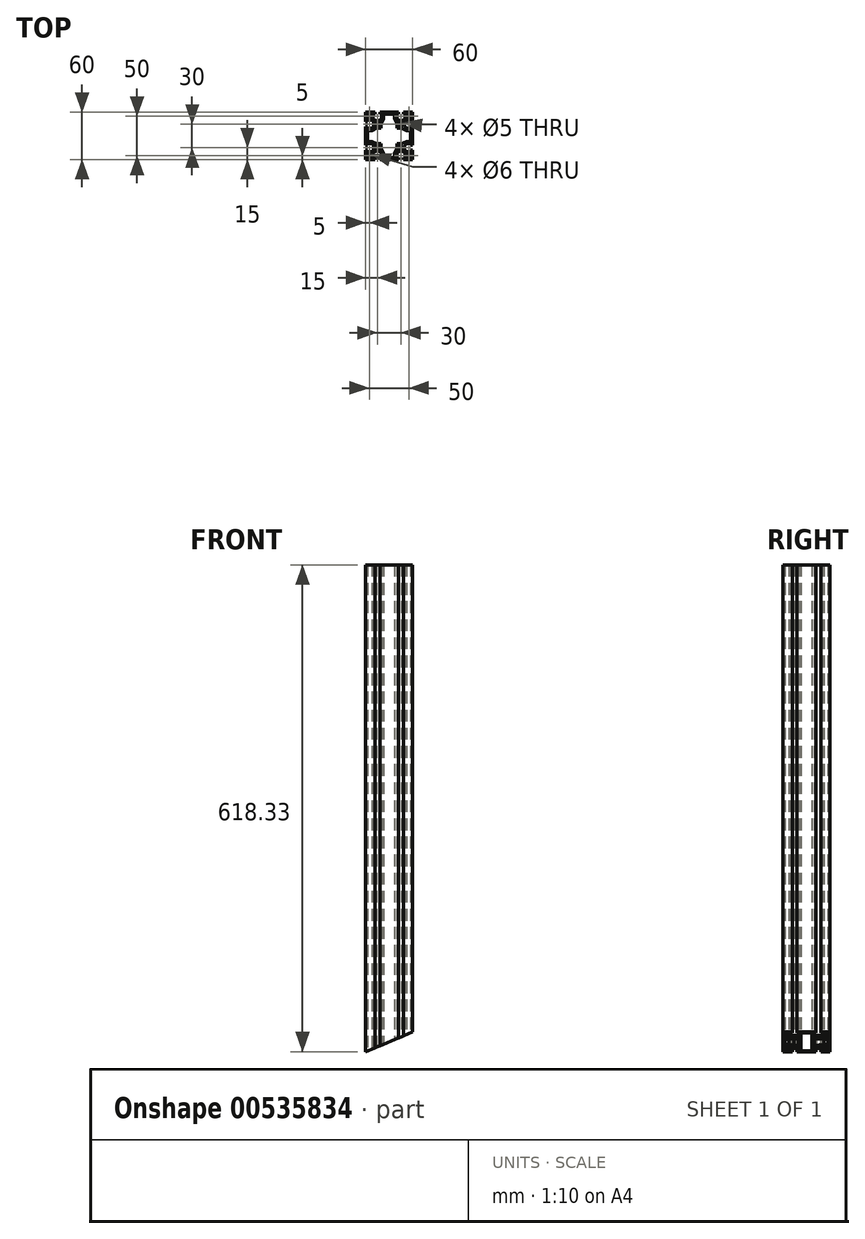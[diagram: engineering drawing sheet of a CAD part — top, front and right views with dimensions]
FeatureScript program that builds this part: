
annotation { "Feature Type Name" : "Feature", "Feature Type Description" : "" }
export const myFeature = defineFeature(function(context is Context, id is Id, definition is map)
    precondition{}
    {
        {
            var Q0;
            Q0=qCreatedBy(makeId("Top.planeOp"),FACE);
            var sketch = newSketch(context, id + "F0", { "sketchPlane" : qUnion([Q0])});
            skLineSegment(sketch, "E0.bottom", {"start": v(30, -30) * mm, "end": v(-30, -30) * mm});
            skLineSegment(sketch, "E0.top", {"start": v(30, 30) * mm, "end": v(-30, 30) * mm});
            skLineSegment(sketch, "E0.left", {"start": v(30, -30) * mm, "end": v(30, 30) * mm});
            skLineSegment(sketch, "E0.right", {"start": v(-30, -30) * mm, "end": v(-30, 30) * mm});
            skPoint(sketch, "E0.middle", {"position": v(0, 0) * mm});
            skLineSegment(sketch, "E1.top", {"start": v(-11.85, 30) * mm, "end": v(-18.15, 30) * mm});
            skLineSegment(sketch, "E1.left", {"start": v(-11.85, 27.5) * mm, "end": v(-11.85, 30) * mm});
            skLineSegment(sketch, "E1.right", {"start": v(-18.15, 27.5) * mm, "end": v(-18.15, 30) * mm});
            skPoint(sketch, "E1.middle", {"position": v(-15, 28.75) * mm});
            skLineSegment(sketch, "E2.bottom", {"start": v(-9.85, 27.5) * mm, "end": v(-11.85, 27.5) * mm});
            skLineSegment(sketch, "E2.left", {"start": v(-9.85, 27.5) * mm, "end": v(-9.85, 21.55) * mm});
            skLineSegment(sketch, "E2.right", {"start": v(-20.15, 27.5) * mm, "end": v(-20.15, 21.55) * mm});
            skPoint(sketch, "E2.middle", {"position": v(-15, 24.52) * mm});
            skArc(sketch, "E3", {"start": v(-20.15, 21.55) * mm, "mid": v(-15, 19.5) * mm, "end": v(-9.85, 21.55) * mm});
            skPoint(sketch, "E4.MirrorP", {"position": v(15, 24.52) * mm});
            skPoint(sketch, "E5.MirrorP", {"position": v(15, 28.75) * mm});
            skLineSegment(sketch, "E6.MirrorCS", {"start": v(11.85, 27.5) * mm, "end": v(11.85, 30) * mm});
            skLineSegment(sketch, "E7.MirrorCS", {"start": v(18.15, 27.5) * mm, "end": v(18.15, 30) * mm});
            skLineSegment(sketch, "E8.MirrorCS", {"start": v(9.85, 27.5) * mm, "end": v(11.85, 27.5) * mm});
            skLineSegment(sketch, "E9.MirrorCS", {"start": v(9.85, 27.5) * mm, "end": v(9.85, 21.55) * mm});
            skArc(sketch, "E10.MirrorCS", {"start": v(20.15, 21.55) * mm, "mid": v(15, 19.5) * mm, "end": v(9.85, 21.55) * mm});
            skLineSegment(sketch, "E11.MirrorCS", {"start": v(20.15, 27.5) * mm, "end": v(20.15, 21.55) * mm});
            skLineSegment(sketch, "E12.MirrorCS", {"start": v(11.85, 30) * mm, "end": v(18.15, 30) * mm});
            skLineSegment(sketch, "E13.1.0", {"start": v(27.5, 20.15) * mm, "end": v(21.55, 20.15) * mm});
            skLineSegment(sketch, "E13.1.1", {"start": v(27.5, 9.85) * mm, "end": v(21.55, 9.85) * mm});
            skArc(sketch, "E13.1.2", {"start": v(21.55, 20.15) * mm, "mid": v(19.5, 15) * mm, "end": v(21.55, 9.85) * mm});
            skLineSegment(sketch, "E13.1.3", {"start": v(27.5, -9.85) * mm, "end": v(21.55, -9.85) * mm});
            skLineSegment(sketch, "E13.1.4", {"start": v(27.5, -20.15) * mm, "end": v(21.55, -20.15) * mm});
            skPoint(sketch, "E13.1.5", {"position": v(28.75, 15) * mm});
            skPoint(sketch, "E13.1.6", {"position": v(28.75, -15) * mm});
            skArc(sketch, "E13.1.7", {"start": v(21.55, -20.15) * mm, "mid": v(19.5, -15) * mm, "end": v(21.55, -9.85) * mm});
            skPoint(sketch, "E13.1.8", {"position": v(24.52, -15) * mm});
            skPoint(sketch, "E13.1.9", {"position": v(24.52, 15) * mm});
            skLineSegment(sketch, "E13.1.10", {"start": v(27.5, 9.85) * mm, "end": v(27.5, 20.15) * mm});
            skLineSegment(sketch, "E13.1.11", {"start": v(27.5, -11.85) * mm, "end": v(27.5, -18.15) * mm});
            skLineSegment(sketch, "E13.1.12", {"start": v(30, 11.85) * mm, "end": v(30, 18.15) * mm});
            skLineSegment(sketch, "E13.1.13", {"start": v(30, -11.85) * mm, "end": v(30, -18.15) * mm});
            skLineSegment(sketch, "E13.1.14", {"start": v(27.5, 18.15) * mm, "end": v(30, 18.15) * mm});
            skLineSegment(sketch, "E13.1.15", {"start": v(27.5, 11.85) * mm, "end": v(30, 11.85) * mm});
            skLineSegment(sketch, "E13.1.16", {"start": v(27.5, 11.85) * mm, "end": v(27.5, 18.15) * mm});
            skLineSegment(sketch, "E13.1.17", {"start": v(27.5, -9.85) * mm, "end": v(27.5, -20.15) * mm});
            skLineSegment(sketch, "E13.1.18", {"start": v(27.5, -18.15) * mm, "end": v(30, -18.15) * mm});
            skLineSegment(sketch, "E13.1.19", {"start": v(27.5, -11.85) * mm, "end": v(30, -11.85) * mm});
            skLineSegment(sketch, "E13.2.0", {"start": v(20.15, -27.5) * mm, "end": v(20.15, -21.55) * mm});
            skLineSegment(sketch, "E13.2.1", {"start": v(9.85, -27.5) * mm, "end": v(9.85, -21.55) * mm});
            skArc(sketch, "E13.2.2", {"start": v(20.15, -21.55) * mm, "mid": v(15, -19.5) * mm, "end": v(9.85, -21.55) * mm});
            skLineSegment(sketch, "E13.2.3", {"start": v(-9.85, -27.5) * mm, "end": v(-9.85, -21.55) * mm});
            skLineSegment(sketch, "E13.2.4", {"start": v(-20.15, -27.5) * mm, "end": v(-20.15, -21.55) * mm});
            skPoint(sketch, "E13.2.5", {"position": v(15, -28.75) * mm});
            skPoint(sketch, "E13.2.6", {"position": v(-15, -28.75) * mm});
            skArc(sketch, "E13.2.7", {"start": v(-20.15, -21.55) * mm, "mid": v(-15, -19.5) * mm, "end": v(-9.85, -21.55) * mm});
            skPoint(sketch, "E13.2.8", {"position": v(-15, -24.52) * mm});
            skPoint(sketch, "E13.2.9", {"position": v(15, -24.52) * mm});
            skLineSegment(sketch, "E13.2.10", {"start": v(9.85, -27.5) * mm, "end": v(20.15, -27.5) * mm});
            skLineSegment(sketch, "E13.2.11", {"start": v(-11.85, -27.5) * mm, "end": v(-18.15, -27.5) * mm});
            skLineSegment(sketch, "E13.2.12", {"start": v(11.85, -30) * mm, "end": v(18.15, -30) * mm});
            skLineSegment(sketch, "E13.2.13", {"start": v(-11.85, -30) * mm, "end": v(-18.15, -30) * mm});
            skLineSegment(sketch, "E13.2.14", {"start": v(18.15, -27.5) * mm, "end": v(18.15, -30) * mm});
            skLineSegment(sketch, "E13.2.15", {"start": v(11.85, -27.5) * mm, "end": v(11.85, -30) * mm});
            skLineSegment(sketch, "E13.2.16", {"start": v(11.85, -27.5) * mm, "end": v(18.15, -27.5) * mm});
            skLineSegment(sketch, "E13.2.17", {"start": v(-9.85, -27.5) * mm, "end": v(-20.15, -27.5) * mm});
            skLineSegment(sketch, "E13.2.18", {"start": v(-18.15, -27.5) * mm, "end": v(-18.15, -30) * mm});
            skLineSegment(sketch, "E13.2.19", {"start": v(-11.85, -27.5) * mm, "end": v(-11.85, -30) * mm});
            skLineSegment(sketch, "E13.3.0", {"start": v(-27.5, -20.15) * mm, "end": v(-21.55, -20.15) * mm});
            skLineSegment(sketch, "E13.3.1", {"start": v(-27.5, -9.85) * mm, "end": v(-21.55, -9.85) * mm});
            skArc(sketch, "E13.3.2", {"start": v(-21.55, -20.15) * mm, "mid": v(-19.5, -15) * mm, "end": v(-21.55, -9.85) * mm});
            skLineSegment(sketch, "E13.3.3", {"start": v(-27.5, 9.85) * mm, "end": v(-21.55, 9.85) * mm});
            skLineSegment(sketch, "E13.3.4", {"start": v(-27.5, 20.15) * mm, "end": v(-21.55, 20.15) * mm});
            skPoint(sketch, "E13.3.5", {"position": v(-28.75, -15) * mm});
            skPoint(sketch, "E13.3.6", {"position": v(-28.75, 15) * mm});
            skArc(sketch, "E13.3.7", {"start": v(-21.55, 20.15) * mm, "mid": v(-19.5, 15) * mm, "end": v(-21.55, 9.85) * mm});
            skPoint(sketch, "E13.3.8", {"position": v(-24.52, 15) * mm});
            skPoint(sketch, "E13.3.9", {"position": v(-24.52, -15) * mm});
            skLineSegment(sketch, "E13.3.10", {"start": v(-27.5, -9.85) * mm, "end": v(-27.5, -20.15) * mm});
            skLineSegment(sketch, "E13.3.11", {"start": v(-27.5, 11.85) * mm, "end": v(-27.5, 18.15) * mm});
            skLineSegment(sketch, "E13.3.12", {"start": v(-30, -11.85) * mm, "end": v(-30, -18.15) * mm});
            skLineSegment(sketch, "E13.3.13", {"start": v(-30, 11.85) * mm, "end": v(-30, 18.15) * mm});
            skLineSegment(sketch, "E13.3.14", {"start": v(-27.5, -18.15) * mm, "end": v(-30, -18.15) * mm});
            skLineSegment(sketch, "E13.3.15", {"start": v(-27.5, -11.85) * mm, "end": v(-30, -11.85) * mm});
            skLineSegment(sketch, "E13.3.16", {"start": v(-27.5, -11.85) * mm, "end": v(-27.5, -18.15) * mm});
            skLineSegment(sketch, "E13.3.17", {"start": v(-27.5, 9.85) * mm, "end": v(-27.5, 20.15) * mm});
            skLineSegment(sketch, "E13.3.18", {"start": v(-27.5, 18.15) * mm, "end": v(-30, 18.15) * mm});
            skLineSegment(sketch, "E13.3.19", {"start": v(-27.5, 11.85) * mm, "end": v(-30, 11.85) * mm});
            skLineSegment(sketch, "E13.anchor1", {"start": v(0, 0) * mm, "end": v(-20.15, 21.55) * mm, "construction": true});
            skLineSegment(sketch, "E13.anchor2", {"start": v(0, 0) * mm, "end": v(-21.55, -20.15) * mm, "construction": true});
            skLineSegment(sketch, "E14.trimOffspring", {"start": v(-18.15, 27.5) * mm, "end": v(-20.15, 27.5) * mm});
            skLineSegment(sketch, "E15.trimOffspring", {"start": v(18.15, 27.5) * mm, "end": v(20.15, 27.5) * mm});
            skCircle(sketch, "E16", {"center": v(-15, 15) * mm, "radius": 2.5 * mm});
            skCircle(sketch, "E17", {"center": v(-25, 25) * mm, "radius": 3 * mm});
            skCircle(sketch, "E18.MirrorC", {"center": v(25, 25) * mm, "radius": 3 * mm});
            skCircle(sketch, "E19.MirrorC", {"center": v(25, -25) * mm, "radius": 3 * mm});
            skCircle(sketch, "E20.MirrorC", {"center": v(-25, -25) * mm, "radius": 3 * mm});
            skCircle(sketch, "E21.MirrorC", {"center": v(15, 15) * mm, "radius": 2.5 * mm});
            skCircle(sketch, "E22.MirrorC", {"center": v(15, -15) * mm, "radius": 2.5 * mm});
            skCircle(sketch, "E23.MirrorC", {"center": v(-15, -15) * mm, "radius": 2.5 * mm});
            skLineSegment(sketch, "E24", {"start": v(-7, 27.5) * mm, "end": v(0, 27.5) * mm});
            skLineSegment(sketch, "E25", {"start": v(-7, 27.5) * mm, "end": v(-7, 22) * mm});
            skLineSegment(sketch, "E26", {"start": v(-10, 10) * mm, "end": v(-10, 16) * mm});
            skLineSegment(sketch, "E27", {"start": v(-10, 16) * mm, "end": v(-7, 22) * mm});
            skLineSegment(sketch, "E28.MirrorCS", {"start": v(10, 10) * mm, "end": v(10, 16) * mm});
            skLineSegment(sketch, "E29.MirrorCS", {"start": v(10, 16) * mm, "end": v(7, 22) * mm});
            skLineSegment(sketch, "E30.MirrorCS", {"start": v(7, 27.5) * mm, "end": v(0, 27.5) * mm});
            skLineSegment(sketch, "E31.MirrorCS", {"start": v(7, 27.5) * mm, "end": v(7, 22) * mm});
            skLineSegment(sketch, "E32.1.0", {"start": v(-10, -10) * mm, "end": v(-16, -10) * mm});
            skLineSegment(sketch, "E32.1.1", {"start": v(-16, -10) * mm, "end": v(-22, -7) * mm});
            skLineSegment(sketch, "E32.1.2", {"start": v(-27.5, -7) * mm, "end": v(-22, -7) * mm});
            skLineSegment(sketch, "E32.1.3", {"start": v(-27.5, -7) * mm, "end": v(-27.5, 0) * mm});
            skLineSegment(sketch, "E32.1.4", {"start": v(-27.5, 7) * mm, "end": v(-27.5, 0) * mm});
            skLineSegment(sketch, "E32.1.5", {"start": v(-27.5, 7) * mm, "end": v(-22, 7) * mm});
            skLineSegment(sketch, "E32.1.6", {"start": v(-16, 10) * mm, "end": v(-22, 7) * mm});
            skLineSegment(sketch, "E32.1.7", {"start": v(-10, 10) * mm, "end": v(-16, 10) * mm});
            skLineSegment(sketch, "E32.2.0", {"start": v(10, -10) * mm, "end": v(10, -16) * mm});
            skLineSegment(sketch, "E32.2.1", {"start": v(10, -16) * mm, "end": v(7, -22) * mm});
            skLineSegment(sketch, "E32.2.2", {"start": v(7, -27.5) * mm, "end": v(7, -22) * mm});
            skLineSegment(sketch, "E32.2.3", {"start": v(7, -27.5) * mm, "end": v(0, -27.5) * mm});
            skLineSegment(sketch, "E32.2.4", {"start": v(-7, -27.5) * mm, "end": v(0, -27.5) * mm});
            skLineSegment(sketch, "E32.2.5", {"start": v(-7, -27.5) * mm, "end": v(-7, -22) * mm});
            skLineSegment(sketch, "E32.2.6", {"start": v(-10, -16) * mm, "end": v(-7, -22) * mm});
            skLineSegment(sketch, "E32.2.7", {"start": v(-10, -10) * mm, "end": v(-10, -16) * mm});
            skLineSegment(sketch, "E32.3.0", {"start": v(10, 10) * mm, "end": v(16, 10) * mm});
            skLineSegment(sketch, "E32.3.1", {"start": v(16, 10) * mm, "end": v(22, 7) * mm});
            skLineSegment(sketch, "E32.3.2", {"start": v(27.5, 7) * mm, "end": v(22, 7) * mm});
            skLineSegment(sketch, "E32.3.3", {"start": v(27.5, 7) * mm, "end": v(27.5, 0) * mm});
            skLineSegment(sketch, "E32.3.4", {"start": v(27.5, -7) * mm, "end": v(27.5, 0) * mm});
            skLineSegment(sketch, "E32.3.5", {"start": v(27.5, -7) * mm, "end": v(22, -7) * mm});
            skLineSegment(sketch, "E32.3.6", {"start": v(16, -10) * mm, "end": v(22, -7) * mm});
            skLineSegment(sketch, "E32.3.7", {"start": v(10, -10) * mm, "end": v(16, -10) * mm});
            skSolve(sketch);
        }
        {
            var Q0;
            {var subQ30=sQuery(id+"F0.wireOp",EDGE,"E1.left");Q0=makeQuery(id+"F0.imprint","IMPRINT",FACE,{"disambiguationData":[TD([[makeQuery(id+"F0.imprint","IMPRINT",EDGE,{"derivedFrom":subQ30}),-1.0]])]});}
            extrude(context, id + "F1", {"entities" : qUnion([Q0]), "depth" : 618.33 * mm, "offsetDistance" : 25 * mm});
        }
        {
            var Q0;
            Q0=makeQuery(id+"F1.opExtrude","SWEPT_EDGE",EDGE,{"disambiguationData":[OSD([sQuery(id+"F0.wireOp",EDGE,"E24"),sQuery(id+"F0.wireOp",EDGE,"E25")])]});
            var Q1;
            Q1=makeQuery(id+"F1.opExtrude","SWEPT_EDGE",EDGE,{"disambiguationData":[OSD([sQuery(id+"F0.wireOp",EDGE,"E30.MirrorCS"),sQuery(id+"F0.wireOp",EDGE,"E31.MirrorCS")])]});
            var Q2;
            Q2=makeQuery(id+"F1.opExtrude","SWEPT_EDGE",EDGE,{"disambiguationData":[OSD([sQuery(id+"F0.wireOp",EDGE,"840db5bc-c403-45cd-90c7-254e62d9e8c5.3.2"),sQuery(id+"F0.wireOp",EDGE,"840db5bc-c403-45cd-90c7-254e62d9e8c5.3.3")])]});
            var Q3;
            Q3=makeQuery(id+"F1.opExtrude","SWEPT_EDGE",EDGE,{"disambiguationData":[OSD([sQuery(id+"F0.wireOp",EDGE,"840db5bc-c403-45cd-90c7-254e62d9e8c5.3.4"),sQuery(id+"F0.wireOp",EDGE,"840db5bc-c403-45cd-90c7-254e62d9e8c5.3.5")])]});
            var Q4;
            Q4=makeQuery(id+"F1.opExtrude","SWEPT_EDGE",EDGE,{"disambiguationData":[OSD([sQuery(id+"F0.wireOp",EDGE,"840db5bc-c403-45cd-90c7-254e62d9e8c5.1.4"),sQuery(id+"F0.wireOp",EDGE,"840db5bc-c403-45cd-90c7-254e62d9e8c5.1.5")])]});
            var Q5;
            Q5=makeQuery(id+"F1.opExtrude","SWEPT_EDGE",EDGE,{"disambiguationData":[OSD([sQuery(id+"F0.wireOp",EDGE,"840db5bc-c403-45cd-90c7-254e62d9e8c5.1.2"),sQuery(id+"F0.wireOp",EDGE,"840db5bc-c403-45cd-90c7-254e62d9e8c5.1.3")])]});
            var Q6;
            Q6=makeQuery(id+"F1.opExtrude","SWEPT_EDGE",EDGE,{"disambiguationData":[OSD([sQuery(id+"F0.wireOp",EDGE,"840db5bc-c403-45cd-90c7-254e62d9e8c5.2.2"),sQuery(id+"F0.wireOp",EDGE,"840db5bc-c403-45cd-90c7-254e62d9e8c5.2.3")])]});
            var Q7;
            Q7=makeQuery(id+"F1.opExtrude","SWEPT_EDGE",EDGE,{"disambiguationData":[OSD([sQuery(id+"F0.wireOp",EDGE,"840db5bc-c403-45cd-90c7-254e62d9e8c5.2.4"),sQuery(id+"F0.wireOp",EDGE,"840db5bc-c403-45cd-90c7-254e62d9e8c5.2.5")])]});
            fillet(context, id + "F2", {"entities" : qUnion([Q0, Q1, Q2, Q3, Q4, Q5, Q6, Q7]), "radius" : 2 * mm, "tangentPropagation" : true, "allowEdgeOverflow" : false});
        }
        {
            var Q0;
            Q0=makeQuery(id+"F1.opExtrude","SWEPT_EDGE",EDGE,{"disambiguationData":[OSD([sQuery(id+"F0.wireOp",EDGE,"E26"),sQuery(id+"F0.wireOp",EDGE,"E27")])]});
            var Q1;
            Q1=makeQuery(id+"F1.opExtrude","SWEPT_EDGE",EDGE,{"disambiguationData":[OSD([sQuery(id+"F0.wireOp",EDGE,"E28.MirrorCS"),sQuery(id+"F0.wireOp",EDGE,"E29.MirrorCS")])]});
            var Q2;
            Q2=makeQuery(id+"F1.opExtrude","SWEPT_EDGE",EDGE,{"disambiguationData":[OSD([sQuery(id+"F0.wireOp",EDGE,"840db5bc-c403-45cd-90c7-254e62d9e8c5.3.0"),sQuery(id+"F0.wireOp",EDGE,"840db5bc-c403-45cd-90c7-254e62d9e8c5.3.1")])]});
            var Q3;
            Q3=makeQuery(id+"F1.opExtrude","SWEPT_EDGE",EDGE,{"disambiguationData":[OSD([sQuery(id+"F0.wireOp",EDGE,"840db5bc-c403-45cd-90c7-254e62d9e8c5.1.6"),sQuery(id+"F0.wireOp",EDGE,"840db5bc-c403-45cd-90c7-254e62d9e8c5.1.7")])]});
            var Q4;
            Q4=makeQuery(id+"F1.opExtrude","SWEPT_EDGE",EDGE,{"disambiguationData":[OSD([sQuery(id+"F0.wireOp",EDGE,"840db5bc-c403-45cd-90c7-254e62d9e8c5.1.0"),sQuery(id+"F0.wireOp",EDGE,"840db5bc-c403-45cd-90c7-254e62d9e8c5.1.1")])]});
            var Q5;
            Q5=makeQuery(id+"F1.opExtrude","SWEPT_EDGE",EDGE,{"disambiguationData":[OSD([sQuery(id+"F0.wireOp",EDGE,"840db5bc-c403-45cd-90c7-254e62d9e8c5.3.6"),sQuery(id+"F0.wireOp",EDGE,"840db5bc-c403-45cd-90c7-254e62d9e8c5.3.7")])]});
            var Q6;
            Q6=makeQuery(id+"F1.opExtrude","SWEPT_EDGE",EDGE,{"disambiguationData":[OSD([sQuery(id+"F0.wireOp",EDGE,"840db5bc-c403-45cd-90c7-254e62d9e8c5.2.0"),sQuery(id+"F0.wireOp",EDGE,"840db5bc-c403-45cd-90c7-254e62d9e8c5.2.1")])]});
            var Q7;
            Q7=makeQuery(id+"F1.opExtrude","SWEPT_EDGE",EDGE,{"disambiguationData":[OSD([sQuery(id+"F0.wireOp",EDGE,"840db5bc-c403-45cd-90c7-254e62d9e8c5.2.6"),sQuery(id+"F0.wireOp",EDGE,"840db5bc-c403-45cd-90c7-254e62d9e8c5.2.7")])]});
            fillet(context, id + "F3", {"entities" : qUnion([Q0, Q1, Q2, Q3, Q4, Q5, Q6, Q7]), "radius" : 7 * mm, "tangentPropagation" : true, "allowEdgeOverflow" : false});
        }
        {
            var Q0;
            Q0=qCreatedBy(makeId("Front.planeOp"),FACE);
            var sketch = newSketch(context, id + "F4", { "sketchPlane" : qUnion([Q0])});
            skLineSegment(sketch, "E33.bottom", {"start": v(-30, 0) * mm, "end": v(227.68, 106.74) * mm});
            skLineSegment(sketch, "E33.top", {"start": v(35.18, -157.35) * mm, "end": v(292.86, -50.61) * mm});
            skLineSegment(sketch, "E33.left", {"start": v(-30, 0) * mm, "end": v(35.18, -157.35) * mm});
            skLineSegment(sketch, "E33.right", {"start": v(227.68, 106.74) * mm, "end": v(292.86, -50.61) * mm});
            skSolve(sketch);
        }
        {
            var Q0;
            Q0 = qSketchRegion(id + "F4", true);
            extrude(context, id + "F5", {"entities" : qUnion([Q0]), "operationType" : NewBodyOperationType.REMOVE, "depth" : 30 * mm, "offsetDistance" : 25 * mm, "hasSecondDirection" : true, "secondDirectionOppositeDirection" : true, "secondDirectionDepth" : 30 * mm});
        }
    });
